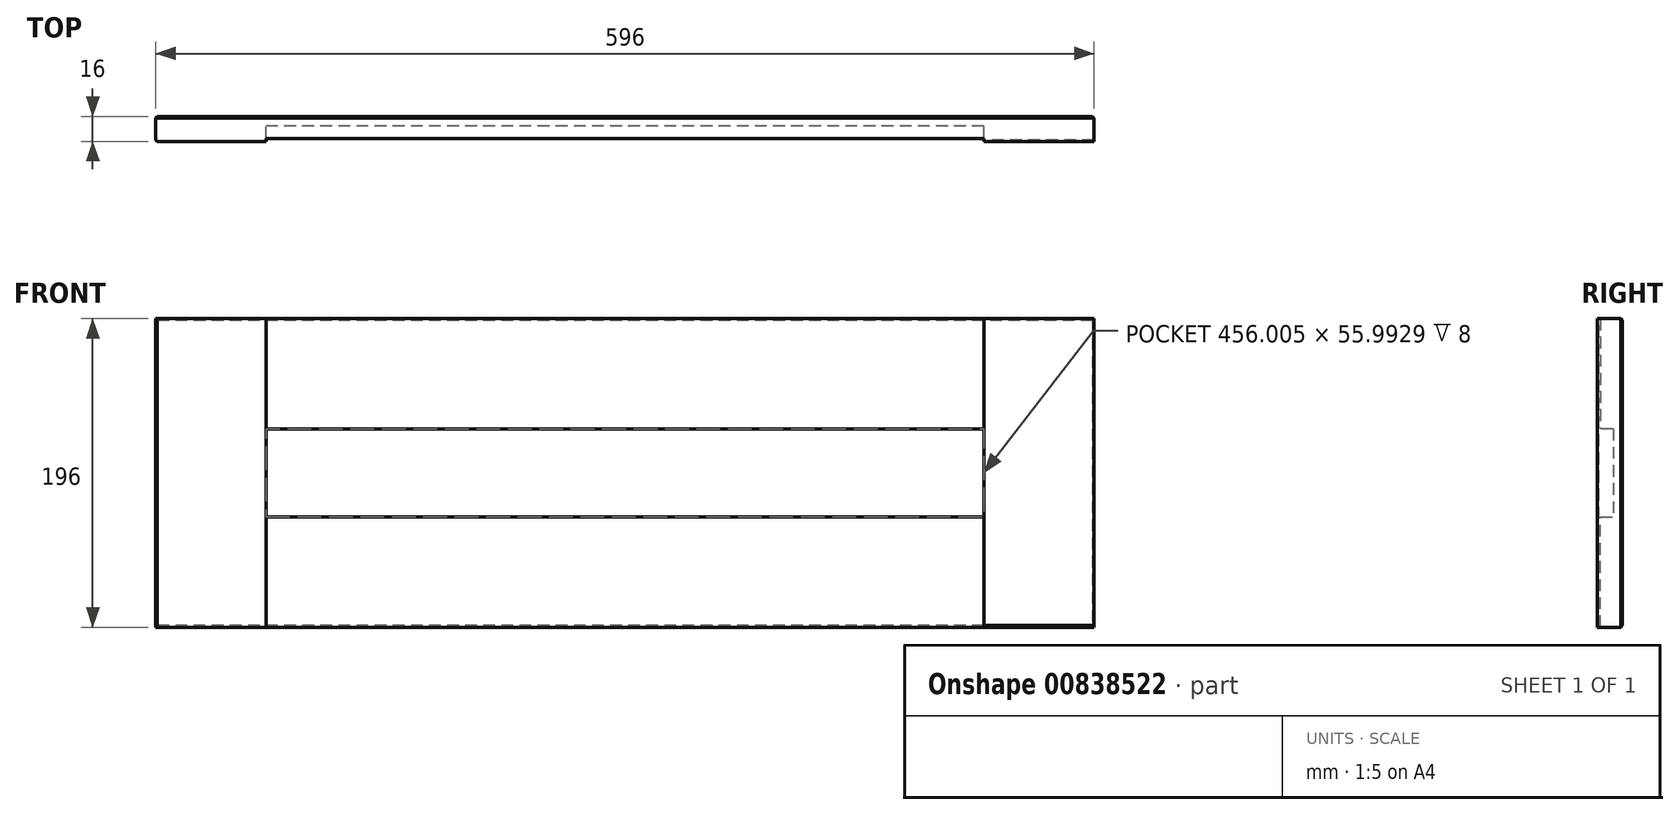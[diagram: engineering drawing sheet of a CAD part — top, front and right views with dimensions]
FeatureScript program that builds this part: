
annotation { "Feature Type Name" : "Feature", "Feature Type Description" : "" }
export const myFeature = defineFeature(function(context is Context, id is Id, definition is map)
    precondition{}
    {
        {
            var Q0;
            Q0=qCreatedBy(makeId("Front.planeOp"),FACE);
            var sketch = newSketch(context, id + "F0", { "sketchPlane" : qUnion([Q0])});
            skLineSegment(sketch, "E0.bottom", {"start": v(0, 0) * mm, "end": v(35.9, 0) * mm});
            skLineSegment(sketch, "E0.top", {"start": v(0, 30.12) * mm, "end": v(35.9, 30.12) * mm});
            skLineSegment(sketch, "E0.left", {"start": v(0, 0) * mm, "end": v(0, 30.12) * mm});
            skLineSegment(sketch, "E0.right", {"start": v(35.9, 0) * mm, "end": v(35.9, 30.12) * mm});
            skSolve(sketch);
        }
        {
            var Q0;
            Q0=makeQuery(id+"F0.imprint","IMPRINT",FACE,{"disambiguationData":[TD([[makeQuery(id+"F0.imprint","IMPRINT",EDGE,{"derivedFrom":sQuery(id+"F0.wireOp",EDGE,"E0.bottom")}),1.0]])]});
            extrude(context, id + "F1", {"entities" : qUnion([Q0]), "depth" : 16 * mm, "offsetDistance" : 25.4 * mm});
        }
        {
            var Q0;
            Q0=makeQuery(id+"F1.opExtrude","SWEPT_FACE",FACE,{"disambiguationData":[OSD([sQuery(id+"F0.wireOp",EDGE,"E0.left")])]});
            extrude(context, id + "F2", {"entities" : qUnion([Q0]), "operationType" : NewBodyOperationType.ADD, "oppositeDirection" : true, "depth" : 196 * mm, "offsetDistance" : 25 * mm});
        }
        {
            var Q0;
            {var subQ0=sQuery(id+"F0.wireOp",EDGE,"E0.bottom");Q0=makeQuery(id+"F2.boolean.opBoolean","MERGE",FACE,{"derivedFrom":[makeQuery(id+"F1.opExtrude","SWEPT_FACE",FACE,{"disambiguationData":[OSD([subQ0])]}),makeQuery(id+"F2.opExtrude","SWEPT_FACE",FACE,{"disambiguationData":[OSD([subQ0,sQuery(id+"F0.wireOp",EDGE,"E0.left")])]})]});}
            extrude(context, id + "F3", {"entities" : qUnion([Q0]), "operationType" : NewBodyOperationType.ADD, "oppositeDirection" : true, "depth" : 796 * mm, "offsetDistance" : 25 * mm});
        }
        {
            var Q0;
            {var subQ0=sQuery(id+"F0.wireOp",EDGE,"E0.left");var subQ1=sQuery(id+"F0.wireOp",EDGE,"E0.bottom");Q0=makeQuery(id+"F3.boolean.opBoolean","MERGE",FACE,{"derivedFrom":[makeQuery(id+"F2.boolean.opBoolean","MERGE",FACE,{"derivedFrom":[makeQuery(id+"F1.opExtrude","CAP_FACE",FACE,{"disambiguationData":[OSD([subQ1,sQuery(id+"F0.wireOp",EDGE,"E0.top"),subQ0,sQuery(id+"F0.wireOp",EDGE,"E0.right")])],"isStart":false}),makeQuery(id+"F2.opExtrude","SWEPT_FACE",FACE,{"disambiguationData":[OSD([subQ0]),TDD([makeQuery(id+"F1.opExtrude","CAP_EDGE",EDGE,{"disambiguationData":[OSD([subQ0])],"isStart":false})])]})]}),makeQuery(id+"F3.opExtrude","SWEPT_FACE",FACE,{"disambiguationData":[OSD([subQ1,subQ0]),TDD([makeQuery(id+"F2.boolean.opBoolean","MERGE",EDGE,{"derivedFrom":[makeQuery(id+"F1.opExtrude","CAP_EDGE",EDGE,{"disambiguationData":[OSD([subQ1])],"isStart":false}),makeQuery(id+"F2.opExtrude","SWEPT_EDGE",EDGE,{"disambiguationData":[OSD([subQ1,subQ0]),TDD([makeQuery(id+"F1.opExtrude","CAP_VERTEX",VERTEX,{"disambiguationData":[OSD([subQ1,subQ0])],"isStart":false})])]})]})])]})]});}
            var sketch = newSketch(context, id + "F4", { "sketchPlane" : qUnion([Q0])});
            skLineSegment(sketch, "E1.bottom", {"start": v(0, 796) * mm, "end": v(42.19, 796) * mm});
            skLineSegment(sketch, "E1.top", {"start": v(0, 751.57) * mm, "end": v(42.19, 751.57) * mm});
            skLineSegment(sketch, "E1.left", {"start": v(0, 796) * mm, "end": v(0, 751.57) * mm});
            skLineSegment(sketch, "E1.right", {"start": v(42.19, 796) * mm, "end": v(42.19, 751.57) * mm});
            skLineSegment(sketch, "E2.bottom", {"start": v(196, 796) * mm, "end": v(153.6, 796) * mm});
            skLineSegment(sketch, "E2.top", {"start": v(196, 746.75) * mm, "end": v(153.6, 746.75) * mm});
            skLineSegment(sketch, "E2.left", {"start": v(196, 796) * mm, "end": v(196, 746.75) * mm});
            skLineSegment(sketch, "E2.right", {"start": v(153.6, 796) * mm, "end": v(153.6, 746.75) * mm});
            skSolve(sketch);
        }
        {
            var Q0;
            Q0=makeQuery(id+"F4.imprint","IMPRINT",FACE,{"disambiguationData":[TD([[makeQuery(id+"F4.imprint","IMPRINT",EDGE,{"derivedFrom":sQuery(id+"F4.wireOp",EDGE,"E1.bottom")}),-1.0]])]});
            var Q1;
            Q1=makeQuery(id+"F4.imprint","IMPRINT",FACE,{"disambiguationData":[TD([[makeQuery(id+"F4.imprint","IMPRINT",EDGE,{"derivedFrom":sQuery(id+"F4.wireOp",EDGE,"E2.bottom")}),-1.0]])]});
            extrude(context, id + "F5", {"entities" : qUnion([Q0, Q1]), "operationType" : NewBodyOperationType.ADD, "depth" : 25 * mm, "offsetDistance" : 25 * mm});
        }
        {
            var Q0;
            {var subQ0=sQuery(id+"F0.wireOp",EDGE,"E0.left");var subQ1=sQuery(id+"F0.wireOp",EDGE,"E0.bottom");Q0=makeQuery(id+"F3.boolean.opBoolean","MERGE",FACE,{"derivedFrom":[makeQuery(id+"F2.boolean.opBoolean","MERGE",FACE,{"derivedFrom":[makeQuery(id+"F1.opExtrude","CAP_FACE",FACE,{"disambiguationData":[OSD([subQ1,sQuery(id+"F0.wireOp",EDGE,"E0.top"),subQ0,sQuery(id+"F0.wireOp",EDGE,"E0.right")])],"isStart":false}),makeQuery(id+"F2.opExtrude","SWEPT_FACE",FACE,{"disambiguationData":[OSD([subQ0]),TDD([makeQuery(id+"F1.opExtrude","CAP_EDGE",EDGE,{"disambiguationData":[OSD([subQ0])],"isStart":false})])]})]}),makeQuery(id+"F3.opExtrude","SWEPT_FACE",FACE,{"disambiguationData":[OSD([subQ1,subQ0]),TDD([makeQuery(id+"F2.boolean.opBoolean","MERGE",EDGE,{"derivedFrom":[makeQuery(id+"F1.opExtrude","CAP_EDGE",EDGE,{"disambiguationData":[OSD([subQ1])],"isStart":false}),makeQuery(id+"F2.opExtrude","SWEPT_EDGE",EDGE,{"disambiguationData":[OSD([subQ1,subQ0]),TDD([makeQuery(id+"F1.opExtrude","CAP_VERTEX",VERTEX,{"disambiguationData":[OSD([subQ1,subQ0])],"isStart":false})])]})]})])]})]});}
            var sketch = newSketch(context, id + "F6", { "sketchPlane" : qUnion([Q0])});
            skLineSegment(sketch, "E3.bottom", {"start": v(196, 0) * mm, "end": v(163.38, 0) * mm});
            skLineSegment(sketch, "E3.top", {"start": v(196, 46.55) * mm, "end": v(163.38, 46.55) * mm});
            skLineSegment(sketch, "E3.left", {"start": v(196, 0) * mm, "end": v(196, 46.55) * mm});
            skLineSegment(sketch, "E3.right", {"start": v(163.38, 0) * mm, "end": v(163.38, 46.55) * mm});
            skLineSegment(sketch, "E4.bottom", {"start": v(0, 0) * mm, "end": v(50.28, 0) * mm});
            skLineSegment(sketch, "E4.top", {"start": v(0, 44.4) * mm, "end": v(50.28, 44.4) * mm});
            skLineSegment(sketch, "E4.left", {"start": v(0, 0) * mm, "end": v(0, 44.4) * mm});
            skLineSegment(sketch, "E4.right", {"start": v(50.28, 0) * mm, "end": v(50.28, 44.4) * mm});
            skSolve(sketch);
        }
        {
            var Q0;
            Q0=makeQuery(id+"F6.imprint","IMPRINT",FACE,{"disambiguationData":[TD([[makeQuery(id+"F6.imprint","IMPRINT",EDGE,{"derivedFrom":sQuery(id+"F6.wireOp",EDGE,"E3.bottom")}),1.0]])]});
            var Q1;
            Q1=makeQuery(id+"F6.imprint","IMPRINT",FACE,{"disambiguationData":[TD([[makeQuery(id+"F6.imprint","IMPRINT",EDGE,{"derivedFrom":sQuery(id+"F6.wireOp",EDGE,"E4.bottom")}),1.0]])]});
            extrude(context, id + "F7", {"entities" : qUnion([Q0, Q1]), "operationType" : NewBodyOperationType.ADD, "depth" : 25 * mm, "offsetDistance" : 25 * mm});
        }
        {
            var Q0;
            Q0=makeQuery(id+"F7.opExtrude","SWEPT_FACE",FACE,{"disambiguationData":[OSD([sQuery(id+"F6.wireOp",EDGE,"E4.right")])]});
            extrude(context, id + "F8", {"entities" : qUnion([Q0]), "operationType" : NewBodyOperationType.ADD, "depth" : 19.72 * mm, "offsetDistance" : 25 * mm});
        }
        {
            var Q0;
            {var subQ0=sQuery(id+"F6.wireOp",EDGE,"E4.top");Q0=makeQuery(id+"F8.boolean.opBoolean","MERGE",FACE,{"derivedFrom":[makeQuery(id+"F7.opExtrude","SWEPT_FACE",FACE,{"disambiguationData":[OSD([subQ0])]}),makeQuery(id+"F8.opExtrude","SWEPT_FACE",FACE,{"disambiguationData":[OSD([subQ0,sQuery(id+"F6.wireOp",EDGE,"E4.right")])]})]});}
            extrude(context, id + "F9", {"entities" : qUnion([Q0]), "operationType" : NewBodyOperationType.ADD, "depth" : 25.6 * mm, "offsetDistance" : 25 * mm});
        }
        {
            var Q0;
            Q0=makeQuery(id+"F7.opExtrude","SWEPT_FACE",FACE,{"disambiguationData":[OSD([sQuery(id+"F6.wireOp",EDGE,"E3.right")])]});
            extrude(context, id + "F10", {"entities" : qUnion([Q0]), "operationType" : NewBodyOperationType.ADD, "depth" : 37.38 * mm, "offsetDistance" : 25 * mm});
        }
        {
            var Q0;
            {var subQ0=sQuery(id+"F6.wireOp",EDGE,"E3.top");Q0=makeQuery(id+"F10.boolean.opBoolean","MERGE",FACE,{"derivedFrom":[makeQuery(id+"F7.opExtrude","SWEPT_FACE",FACE,{"disambiguationData":[OSD([subQ0])]}),makeQuery(id+"F10.opExtrude","SWEPT_FACE",FACE,{"disambiguationData":[OSD([subQ0,sQuery(id+"F6.wireOp",EDGE,"E3.right")])]})]});}
            extrude(context, id + "F11", {"entities" : qUnion([Q0]), "operationType" : NewBodyOperationType.ADD, "depth" : 23.45 * mm, "offsetDistance" : 25 * mm});
        }
        {
            var Q0;
            Q0=makeQuery(id+"F5.opExtrude","SWEPT_FACE",FACE,{"disambiguationData":[OSD([sQuery(id+"F4.wireOp",EDGE,"E1.right")])]});
            extrude(context, id + "F12", {"entities" : qUnion([Q0]), "operationType" : NewBodyOperationType.ADD, "depth" : 27.8 * mm, "offsetDistance" : 25 * mm});
        }
        {
            var Q0;
            {var subQ0=sQuery(id+"F4.wireOp",EDGE,"E1.top");Q0=makeQuery(id+"F12.boolean.opBoolean","MERGE",FACE,{"derivedFrom":[makeQuery(id+"F5.opExtrude","SWEPT_FACE",FACE,{"disambiguationData":[OSD([subQ0])]}),makeQuery(id+"F12.opExtrude","SWEPT_FACE",FACE,{"disambiguationData":[OSD([subQ0,sQuery(id+"F4.wireOp",EDGE,"E1.right")])]})]});}
            extrude(context, id + "F13", {"entities" : qUnion([Q0]), "operationType" : NewBodyOperationType.ADD, "depth" : 25.57 * mm, "offsetDistance" : 25 * mm});
        }
        {
            var Q0;
            Q0=makeQuery(id+"F5.opExtrude","SWEPT_FACE",FACE,{"disambiguationData":[OSD([sQuery(id+"F4.wireOp",EDGE,"E2.top")])]});
            extrude(context, id + "F14", {"entities" : qUnion([Q0]), "operationType" : NewBodyOperationType.ADD, "depth" : 20.75 * mm, "offsetDistance" : 25 * mm});
        }
        {
            var Q0;
            {var subQ0=sQuery(id+"F4.wireOp",EDGE,"E2.right");Q0=makeQuery(id+"F14.boolean.opBoolean","MERGE",FACE,{"derivedFrom":[makeQuery(id+"F5.opExtrude","SWEPT_FACE",FACE,{"disambiguationData":[OSD([subQ0])]}),makeQuery(id+"F14.opExtrude","SWEPT_FACE",FACE,{"disambiguationData":[OSD([sQuery(id+"F4.wireOp",EDGE,"E2.top"),subQ0])]})]});}
            extrude(context, id + "F15", {"entities" : qUnion([Q0]), "operationType" : NewBodyOperationType.ADD, "depth" : 27.6 * mm, "offsetDistance" : 25 * mm});
        }
        {
            var Q0;
            {var subQ0=sQuery(id+"F0.wireOp",EDGE,"E0.left");var subQ1=sQuery(id+"F0.wireOp",EDGE,"E0.bottom");Q0=makeQuery(id+"F3.boolean.opBoolean","MERGE",FACE,{"derivedFrom":[makeQuery(id+"F2.boolean.opBoolean","MERGE",FACE,{"derivedFrom":[makeQuery(id+"F1.opExtrude","CAP_FACE",FACE,{"disambiguationData":[OSD([subQ1,sQuery(id+"F0.wireOp",EDGE,"E0.top"),subQ0,sQuery(id+"F0.wireOp",EDGE,"E0.right")])],"isStart":false}),makeQuery(id+"F2.opExtrude","SWEPT_FACE",FACE,{"disambiguationData":[OSD([subQ0]),TDD([makeQuery(id+"F1.opExtrude","CAP_EDGE",EDGE,{"disambiguationData":[OSD([subQ0])],"isStart":false})])]})]}),makeQuery(id+"F3.opExtrude","SWEPT_FACE",FACE,{"disambiguationData":[OSD([subQ1,subQ0]),TDD([makeQuery(id+"F2.boolean.opBoolean","MERGE",EDGE,{"derivedFrom":[makeQuery(id+"F1.opExtrude","CAP_EDGE",EDGE,{"disambiguationData":[OSD([subQ1])],"isStart":false}),makeQuery(id+"F2.opExtrude","SWEPT_EDGE",EDGE,{"disambiguationData":[OSD([subQ1,subQ0]),TDD([makeQuery(id+"F1.opExtrude","CAP_VERTEX",VERTEX,{"disambiguationData":[OSD([subQ1,subQ0])],"isStart":false})])]})]})])]})]});}
            var sketch = newSketch(context, id + "F16", { "sketchPlane" : qUnion([Q0])});
            skLineSegment(sketch, "E5.bottom", {"start": v(70, 726) * mm, "end": v(126, 726) * mm});
            skLineSegment(sketch, "E5.top", {"start": v(70, 70) * mm, "end": v(126, 70) * mm});
            skLineSegment(sketch, "E5.left", {"start": v(70, 726) * mm, "end": v(70, 70) * mm});
            skLineSegment(sketch, "E5.right", {"start": v(126, 726) * mm, "end": v(126, 70) * mm});
            skSolve(sketch);
        }
        {
            var Q0;
            Q0=makeQuery(id+"F16.imprint","IMPRINT",FACE,{"disambiguationData":[TD([[makeQuery(id+"F16.imprint","IMPRINT",EDGE,{"derivedFrom":sQuery(id+"F16.wireOp",EDGE,"E5.top")}),1.0]])]});
            extrude(context, id + "F17", {"entities" : qUnion([Q0]), "operationType" : NewBodyOperationType.REMOVE, "oppositeDirection" : true, "depth" : 10 * mm, "offsetDistance" : 25 * mm});
        }
        {
            var Q0;
            {var subQ2=sQuery(id+"F0.wireOp",EDGE,"E0.left");var subQ3=sQuery(id+"F0.wireOp",EDGE,"E0.bottom");var subQ4=makeQuery(id+"F1.opExtrude","CAP_FACE",FACE,{"disambiguationData":[OSD([subQ3,sQuery(id+"F0.wireOp",EDGE,"E0.top"),subQ2,sQuery(id+"F0.wireOp",EDGE,"E0.right")])],"isStart":false});var subQ7=makeQuery(id+"F3.opExtrude","SWEPT_FACE",FACE,{"disambiguationData":[OSD([subQ3,subQ2]),TDD([makeQuery(id+"F2.boolean.opBoolean","MERGE",EDGE,{"derivedFrom":[makeQuery(id+"F1.opExtrude","CAP_EDGE",EDGE,{"disambiguationData":[OSD([subQ3])],"isStart":false}),makeQuery(id+"F2.opExtrude","SWEPT_EDGE",EDGE,{"disambiguationData":[OSD([subQ3,subQ2]),TDD([makeQuery(id+"F1.opExtrude","CAP_VERTEX",VERTEX,{"disambiguationData":[OSD([subQ3,subQ2])],"isStart":false})])]})]})])]});var subQ8=makeQuery(id+"F2.opExtrude","SWEPT_FACE",FACE,{"disambiguationData":[OSD([subQ2]),TDD([makeQuery(id+"F1.opExtrude","CAP_EDGE",EDGE,{"disambiguationData":[OSD([subQ2])],"isStart":false})])]});Q0=makeQuery(id+"F17.boolean.opBoolean","SPLIT",FACE,{"disambiguationData":[TD([makeQuery(id+"F1.opExtrude","SWEPT_FACE",FACE,{"disambiguationData":[OSD([subQ3])]})])],"derivedFrom":makeQuery(id+"F3.boolean.opBoolean","MERGE",FACE,{"derivedFrom":[makeQuery(id+"F2.boolean.opBoolean","MERGE",FACE,{"derivedFrom":[subQ4,subQ8]}),subQ7]})});}
            var Q1;
            {var subQ2=sQuery(id+"F4.wireOp",EDGE,"E1.bottom");var subQ3=sQuery(id+"F0.wireOp",EDGE,"E0.left");var subQ4=sQuery(id+"F0.wireOp",EDGE,"E0.bottom");var subQ6=makeQuery(id+"F1.opExtrude","CAP_FACE",FACE,{"disambiguationData":[OSD([subQ4,sQuery(id+"F0.wireOp",EDGE,"E0.top"),subQ3,sQuery(id+"F0.wireOp",EDGE,"E0.right")])],"isStart":false});var subQ7=makeQuery(id+"F2.opExtrude","SWEPT_FACE",FACE,{"disambiguationData":[OSD([subQ3]),TDD([makeQuery(id+"F1.opExtrude","CAP_EDGE",EDGE,{"disambiguationData":[OSD([subQ3])],"isStart":false})])]});var subQ8=makeQuery(id+"F3.opExtrude","SWEPT_FACE",FACE,{"disambiguationData":[OSD([subQ4,subQ3]),TDD([makeQuery(id+"F2.boolean.opBoolean","MERGE",EDGE,{"derivedFrom":[makeQuery(id+"F1.opExtrude","CAP_EDGE",EDGE,{"disambiguationData":[OSD([subQ4])],"isStart":false}),makeQuery(id+"F2.opExtrude","SWEPT_EDGE",EDGE,{"disambiguationData":[OSD([subQ4,subQ3]),TDD([makeQuery(id+"F1.opExtrude","CAP_VERTEX",VERTEX,{"disambiguationData":[OSD([subQ4,subQ3])],"isStart":false})])]})]})])]});Q1=makeQuery(id+"F17.boolean.opBoolean","SPLIT",FACE,{"disambiguationData":[TD([makeQuery(id+"F5.opExtrude","SWEPT_FACE",FACE,{"disambiguationData":[OSD([subQ2])]})])],"derivedFrom":makeQuery(id+"F3.boolean.opBoolean","MERGE",FACE,{"derivedFrom":[makeQuery(id+"F2.boolean.opBoolean","MERGE",FACE,{"derivedFrom":[subQ6,subQ7]}),subQ8]})});}
            extrude(context, id + "F18", {"entities" : qUnion([Q0, Q1]), "operationType" : NewBodyOperationType.REMOVE, "oppositeDirection" : true, "depth" : 2 * mm, "offsetDistance" : 25 * mm});
        }
        {
            var Q0;
            {var subQ0=sQuery(id+"F4.wireOp",EDGE,"E1.right");var subQ1=sQuery(id+"F4.wireOp",EDGE,"E1.top");Q0=makeQuery(id+"F13.boolean.opBoolean","MERGE",FACE,{"derivedFrom":[makeQuery(id+"F12.boolean.opBoolean","MERGE",FACE,{"derivedFrom":[makeQuery(id+"F5.opExtrude","CAP_FACE",FACE,{"disambiguationData":[OSD([sQuery(id+"F4.wireOp",EDGE,"E1.bottom"),subQ1,sQuery(id+"F4.wireOp",EDGE,"E1.left"),subQ0])],"isStart":false}),makeQuery(id+"F12.opExtrude","SWEPT_FACE",FACE,{"disambiguationData":[OSD([subQ0]),TDD([makeQuery(id+"F5.opExtrude","CAP_EDGE",EDGE,{"disambiguationData":[OSD([subQ0])],"isStart":false})])]})]}),makeQuery(id+"F13.opExtrude","SWEPT_FACE",FACE,{"disambiguationData":[OSD([subQ1,subQ0]),TDD([makeQuery(id+"F12.boolean.opBoolean","MERGE",EDGE,{"derivedFrom":[makeQuery(id+"F5.opExtrude","CAP_EDGE",EDGE,{"disambiguationData":[OSD([subQ1])],"isStart":false}),makeQuery(id+"F12.opExtrude","SWEPT_EDGE",EDGE,{"disambiguationData":[OSD([subQ1,subQ0]),TDD([makeQuery(id+"F5.opExtrude","CAP_VERTEX",VERTEX,{"disambiguationData":[OSD([subQ1,subQ0])],"isStart":false})])]})]})])]})]});}
            var Q1;
            {var subQ0=sQuery(id+"F4.wireOp",EDGE,"E2.right");var subQ1=sQuery(id+"F4.wireOp",EDGE,"E2.top");Q1=makeQuery(id+"F15.boolean.opBoolean","MERGE",FACE,{"derivedFrom":[makeQuery(id+"F14.boolean.opBoolean","MERGE",FACE,{"derivedFrom":[makeQuery(id+"F5.opExtrude","CAP_FACE",FACE,{"disambiguationData":[OSD([sQuery(id+"F4.wireOp",EDGE,"E2.bottom"),subQ1,sQuery(id+"F4.wireOp",EDGE,"E2.left"),subQ0])],"isStart":false}),makeQuery(id+"F14.opExtrude","SWEPT_FACE",FACE,{"disambiguationData":[OSD([subQ1]),TDD([makeQuery(id+"F5.opExtrude","CAP_EDGE",EDGE,{"disambiguationData":[OSD([subQ1])],"isStart":false})])]})]}),makeQuery(id+"F15.opExtrude","SWEPT_FACE",FACE,{"disambiguationData":[OSD([subQ1,subQ0]),TDD([makeQuery(id+"F14.boolean.opBoolean","MERGE",EDGE,{"derivedFrom":[makeQuery(id+"F5.opExtrude","CAP_EDGE",EDGE,{"disambiguationData":[OSD([subQ0])],"isStart":false}),makeQuery(id+"F14.opExtrude","SWEPT_EDGE",EDGE,{"disambiguationData":[OSD([subQ1,subQ0]),TDD([makeQuery(id+"F5.opExtrude","CAP_VERTEX",VERTEX,{"disambiguationData":[OSD([subQ1,subQ0])],"isStart":false})])]})]})])]})]});}
            var Q2;
            {var subQ0=sQuery(id+"F6.wireOp",EDGE,"E4.right");var subQ1=sQuery(id+"F6.wireOp",EDGE,"E4.top");Q2=makeQuery(id+"F9.boolean.opBoolean","MERGE",FACE,{"derivedFrom":[makeQuery(id+"F8.boolean.opBoolean","MERGE",FACE,{"derivedFrom":[makeQuery(id+"F7.opExtrude","CAP_FACE",FACE,{"disambiguationData":[OSD([sQuery(id+"F6.wireOp",EDGE,"E4.bottom"),subQ1,sQuery(id+"F6.wireOp",EDGE,"E4.left"),subQ0])],"isStart":false}),makeQuery(id+"F8.opExtrude","SWEPT_FACE",FACE,{"disambiguationData":[OSD([subQ0]),TDD([makeQuery(id+"F7.opExtrude","CAP_EDGE",EDGE,{"disambiguationData":[OSD([subQ0])],"isStart":false})])]})]}),makeQuery(id+"F9.opExtrude","SWEPT_FACE",FACE,{"disambiguationData":[OSD([subQ1,subQ0]),TDD([makeQuery(id+"F8.boolean.opBoolean","MERGE",EDGE,{"derivedFrom":[makeQuery(id+"F7.opExtrude","CAP_EDGE",EDGE,{"disambiguationData":[OSD([subQ1])],"isStart":false}),makeQuery(id+"F8.opExtrude","SWEPT_EDGE",EDGE,{"disambiguationData":[OSD([subQ1,subQ0]),TDD([makeQuery(id+"F7.opExtrude","CAP_VERTEX",VERTEX,{"disambiguationData":[OSD([subQ1,subQ0])],"isStart":false})])]})]})])]})]});}
            var Q3;
            {var subQ0=sQuery(id+"F6.wireOp",EDGE,"E3.right");var subQ1=sQuery(id+"F6.wireOp",EDGE,"E3.top");Q3=makeQuery(id+"F11.boolean.opBoolean","MERGE",FACE,{"derivedFrom":[makeQuery(id+"F10.boolean.opBoolean","MERGE",FACE,{"derivedFrom":[makeQuery(id+"F7.opExtrude","CAP_FACE",FACE,{"disambiguationData":[OSD([sQuery(id+"F6.wireOp",EDGE,"E3.bottom"),subQ1,sQuery(id+"F6.wireOp",EDGE,"E3.left"),subQ0])],"isStart":false}),makeQuery(id+"F10.opExtrude","SWEPT_FACE",FACE,{"disambiguationData":[OSD([subQ0]),TDD([makeQuery(id+"F7.opExtrude","CAP_EDGE",EDGE,{"disambiguationData":[OSD([subQ0])],"isStart":false})])]})]}),makeQuery(id+"F11.opExtrude","SWEPT_FACE",FACE,{"disambiguationData":[OSD([subQ1,subQ0]),TDD([makeQuery(id+"F10.boolean.opBoolean","MERGE",EDGE,{"derivedFrom":[makeQuery(id+"F7.opExtrude","CAP_EDGE",EDGE,{"disambiguationData":[OSD([subQ1])],"isStart":false}),makeQuery(id+"F10.opExtrude","SWEPT_EDGE",EDGE,{"disambiguationData":[OSD([subQ1,subQ0]),TDD([makeQuery(id+"F7.opExtrude","CAP_VERTEX",VERTEX,{"disambiguationData":[OSD([subQ1,subQ0])],"isStart":false})])]})]})])]})]});}
            extrude(context, id + "F19", {"entities" : qUnion([Q0, Q1, Q2, Q3]), "operationType" : NewBodyOperationType.REMOVE, "oppositeDirection" : true, "depth" : 25 * mm, "offsetDistance" : 25 * mm});
        }
        {
            var Q0;
            {var subQ0=sQuery(id+"F4.wireOp",EDGE,"E2.left");var subQ1=sQuery(id+"F0.wireOp",EDGE,"E0.left");var subQ2=sQuery(id+"F0.wireOp",EDGE,"E0.bottom");var subQ3=sQuery(id+"F6.wireOp",EDGE,"E3.left");Q0=makeQuery(id+"F14.boolean.opBoolean","MERGE",FACE,{"derivedFrom":[makeQuery(id+"F11.boolean.opBoolean","MERGE",FACE,{"derivedFrom":[makeQuery(id+"F7.boolean.opBoolean","MERGE",FACE,{"derivedFrom":[makeQuery(id+"F5.boolean.opBoolean","MERGE",FACE,{"derivedFrom":[makeQuery(id+"F3.boolean.opBoolean","MERGE",FACE,{"derivedFrom":[makeQuery(id+"F2.opExtrude","CAP_FACE",FACE,{"disambiguationData":[OSD([subQ1])],"isStart":false}),makeQuery(id+"F3.opExtrude","SWEPT_FACE",FACE,{"disambiguationData":[OSD([subQ2,subQ1]),TDD([makeQuery(id+"F2.opExtrude","CAP_EDGE",EDGE,{"disambiguationData":[OSD([subQ2,subQ1])],"isStart":false})])]})]}),makeQuery(id+"F5.opExtrude","SWEPT_FACE",FACE,{"disambiguationData":[OSD([subQ0])]})]}),makeQuery(id+"F7.opExtrude","SWEPT_FACE",FACE,{"disambiguationData":[OSD([subQ3])]})]}),makeQuery(id+"F11.opExtrude","SWEPT_FACE",FACE,{"disambiguationData":[OSD([subQ2,subQ1,sQuery(id+"F6.wireOp",EDGE,"E3.top"),subQ3])]})]}),makeQuery(id+"F14.opExtrude","SWEPT_FACE",FACE,{"disambiguationData":[OSD([subQ2,subQ1,sQuery(id+"F4.wireOp",EDGE,"E2.top"),subQ0])]})]});}
            extrude(context, id + "F20", {"entities" : qUnion([Q0]), "operationType" : NewBodyOperationType.ADD, "depth" : 200 * mm, "offsetDistance" : 25 * mm});
        }
        {
            var Q0;
            {var subQ0=sQuery(id+"F4.wireOp",EDGE,"E2.right");var subQ1=sQuery(id+"F4.wireOp",EDGE,"E2.top");Q0=makeQuery(id+"F18.boolean.opBoolean","MERGE",FACE,{"derivedFrom":[makeQuery(id+"F15.opExtrude","CAP_FACE",FACE,{"disambiguationData":[OSD([subQ1,subQ0])],"isStart":false}),makeQuery(id+"F18.opExtrude","SWEPT_FACE",FACE,{"disambiguationData":[OSD([subQ1,subQ0])]})]});}
            var Q1;
            {var subQ0=sQuery(id+"F6.wireOp",EDGE,"E3.right");var subQ1=sQuery(id+"F6.wireOp",EDGE,"E3.top");Q1=makeQuery(id+"F18.boolean.opBoolean","MERGE",FACE,{"derivedFrom":[makeQuery(id+"F11.boolean.opBoolean","MERGE",FACE,{"derivedFrom":[makeQuery(id+"F10.opExtrude","CAP_FACE",FACE,{"disambiguationData":[OSD([subQ0])],"isStart":false}),makeQuery(id+"F11.opExtrude","SWEPT_FACE",FACE,{"disambiguationData":[OSD([subQ1,subQ0]),TDD([makeQuery(id+"F10.opExtrude","CAP_EDGE",EDGE,{"disambiguationData":[OSD([subQ1,subQ0])],"isStart":false})])]})]}),makeQuery(id+"F17.boolean.opBoolean","COPY",FACE,{"derivedFrom":makeQuery(id+"F17.opExtrude","SWEPT_FACE",FACE,{"disambiguationData":[OSD([sQuery(id+"F16.wireOp",EDGE,"E5.right")])]})}),makeQuery(id+"F18.opExtrude","SWEPT_FACE",FACE,{"disambiguationData":[OSD([subQ1,subQ0])]})]});}
            extrude(context, id + "F21", {"entities" : qUnion([Q0, Q1]), "operationType" : NewBodyOperationType.REMOVE, "oppositeDirection" : true, "depth" : 200 * mm, "offsetDistance" : 25 * mm});
        }
        {
            var Q0;
            {var subQ0=sQuery(id+"F4.wireOp",EDGE,"E2.bottom");var subQ1=sQuery(id+"F0.wireOp",EDGE,"E0.left");var subQ2=sQuery(id+"F0.wireOp",EDGE,"E0.bottom");var subQ3=sQuery(id+"F4.wireOp",EDGE,"E1.bottom");Q0=makeQuery(id+"F20.boolean.opBoolean","MERGE",FACE,{"derivedFrom":[makeQuery(id+"F15.boolean.opBoolean","MERGE",FACE,{"derivedFrom":[makeQuery(id+"F12.boolean.opBoolean","MERGE",FACE,{"derivedFrom":[makeQuery(id+"F5.boolean.opBoolean","MERGE",FACE,{"derivedFrom":[makeQuery(id+"F3.opExtrude","CAP_FACE",FACE,{"disambiguationData":[OSD([subQ2,subQ1])],"isStart":false}),makeQuery(id+"F5.opExtrude","SWEPT_FACE",FACE,{"disambiguationData":[OSD([subQ3])]}),makeQuery(id+"F5.opExtrude","SWEPT_FACE",FACE,{"disambiguationData":[OSD([subQ0])]})]}),makeQuery(id+"F12.opExtrude","SWEPT_FACE",FACE,{"disambiguationData":[OSD([subQ2,subQ1,subQ3,sQuery(id+"F4.wireOp",EDGE,"E1.right")])]})]}),makeQuery(id+"F15.opExtrude","SWEPT_FACE",FACE,{"disambiguationData":[OSD([subQ2,subQ1,subQ0,sQuery(id+"F4.wireOp",EDGE,"E2.right")])]})]}),makeQuery(id+"F20.opExtrude","SWEPT_FACE",FACE,{"disambiguationData":[OSD([subQ2,subQ1,subQ0,sQuery(id+"F4.wireOp",EDGE,"E2.left")])]})]});}
            extrude(context, id + "F22", {"entities" : qUnion([Q0]), "operationType" : NewBodyOperationType.ADD, "depth" : 200 * mm, "offsetDistance" : 25 * mm});
        }
        {
            var Q0;
            Q0=makeQuery(id+"F17.boolean.opBoolean","COPY",FACE,{"derivedFrom":makeQuery(id+"F17.opExtrude","SWEPT_FACE",FACE,{"disambiguationData":[OSD([sQuery(id+"F16.wireOp",EDGE,"E5.bottom")])]})});
            var Q1;
            {var subQ0=sQuery(id+"F16.wireOp",EDGE,"E5.right");var subQ1=sQuery(id+"F16.wireOp",EDGE,"E5.bottom");var subQ2=sQuery(id+"F4.wireOp",EDGE,"E2.right");var subQ3=sQuery(id+"F4.wireOp",EDGE,"E2.top");var subQ4=makeQuery(id+"F17.boolean.opBoolean","COPY",EDGE,{"derivedFrom":makeQuery(id+"F17.opExtrude","SWEPT_EDGE",EDGE,{"disambiguationData":[OSD([subQ3,subQ2,subQ1,subQ0])]})});Q1=makeQuery(id+"F21.boolean.opBoolean","COPY",FACE,{"derivedFrom":makeQuery(id+"F21.opExtrude","SWEPT_FACE",FACE,{"disambiguationData":[OSD([subQ3,subQ2,subQ1,subQ0]),TDD([makeQuery(id+"F18.boolean.opBoolean","MERGE",EDGE,{"derivedFrom":[subQ4,makeQuery(id+"F18.opExtrude","SWEPT_EDGE",EDGE,{"disambiguationData":[OSD([subQ3,subQ2,subQ1,subQ0])]})]}),makeQuery(id+"F18.boolean.opBoolean","SPLIT",EDGE,{"derivedFrom":subQ4})])]})});}
            extrude(context, id + "F23", {"entities" : qUnion([Q0, Q1]), "operationType" : NewBodyOperationType.REMOVE, "oppositeDirection" : true, "depth" : 200 * mm, "offsetDistance" : 25 * mm});
        }
        {
            var Q0;
            Q0=makeQuery(id+"F23.boolean.opBoolean","COPY",FACE,{"derivedFrom":makeQuery(id+"F23.opExtrude","CAP_FACE",FACE,{"disambiguationData":[OSD([sQuery(id+"F16.wireOp",EDGE,"E5.bottom")])],"isStart":false})});
            var Q1;
            Q1=makeQuery(id+"F23.boolean.opBoolean","COPY",FACE,{"derivedFrom":makeQuery(id+"F23.opExtrude","CAP_FACE",FACE,{"disambiguationData":[OSD([sQuery(id+"F4.wireOp",EDGE,"E2.top"),sQuery(id+"F4.wireOp",EDGE,"E2.right"),sQuery(id+"F16.wireOp",EDGE,"E5.bottom"),sQuery(id+"F16.wireOp",EDGE,"E5.right")])],"isStart":false})});
            extrude(context, id + "F24", {"entities" : qUnion([Q0, Q1]), "operationType" : NewBodyOperationType.ADD, "depth" : 600 * mm, "offsetDistance" : 25 * mm});
        }
        {
            var Q0;
            Q0=makeQuery(id+"F22.opExtrude","CAP_FACE",FACE,{"disambiguationData":[OSD([sQuery(id+"F0.wireOp",EDGE,"E0.bottom"),sQuery(id+"F0.wireOp",EDGE,"E0.left"),sQuery(id+"F4.wireOp",EDGE,"E1.bottom"),sQuery(id+"F4.wireOp",EDGE,"E1.right"),sQuery(id+"F4.wireOp",EDGE,"E2.bottom"),sQuery(id+"F4.wireOp",EDGE,"E2.left"),sQuery(id+"F4.wireOp",EDGE,"E2.right")])],"isStart":false});
            extrude(context, id + "F25", {"entities" : qUnion([Q0]), "operationType" : NewBodyOperationType.REMOVE, "oppositeDirection" : true, "depth" : 600 * mm, "offsetDistance" : 25 * mm, "hasDraft" : true, "draftAngle" : 3 * degree});
        }
        {
            var Q0;
            {var subQ0=sQuery(id+"F4.wireOp",EDGE,"E2.left");var subQ1=sQuery(id+"F0.wireOp",EDGE,"E0.left");var subQ2=sQuery(id+"F0.wireOp",EDGE,"E0.bottom");Q0=makeQuery(id+"F22.boolean.opBoolean","MERGE",FACE,{"derivedFrom":[makeQuery(id+"F20.opExtrude","CAP_FACE",FACE,{"disambiguationData":[OSD([subQ2,subQ1,sQuery(id+"F4.wireOp",EDGE,"E2.top"),subQ0,sQuery(id+"F6.wireOp",EDGE,"E3.top"),sQuery(id+"F6.wireOp",EDGE,"E3.left")])],"isStart":false}),makeQuery(id+"F22.opExtrude","SWEPT_FACE",FACE,{"disambiguationData":[OSD([subQ2,subQ1,sQuery(id+"F4.wireOp",EDGE,"E2.bottom"),subQ0])]})]});}
            extrude(context, id + "F26", {"entities" : qUnion([Q0]), "operationType" : NewBodyOperationType.ADD, "depth" : 200 * mm, "offsetDistance" : 25 * mm, "hasSecondDirection" : true, "secondDirectionOppositeDirection" : true, "secondDirectionDepth" : 25 * mm});
        }
        {
            var Q0;
            {var subQ0=sQuery(id+"F16.wireOp",EDGE,"E5.right");var subQ1=sQuery(id+"F16.wireOp",EDGE,"E5.bottom");var subQ2=sQuery(id+"F4.wireOp",EDGE,"E2.right");var subQ3=sQuery(id+"F4.wireOp",EDGE,"E2.top");var subQ4=makeQuery(id+"F17.boolean.opBoolean","COPY",EDGE,{"derivedFrom":makeQuery(id+"F17.opExtrude","SWEPT_EDGE",EDGE,{"disambiguationData":[OSD([subQ3,subQ2,subQ1,subQ0])]})});Q0=makeQuery(id+"F23.boolean.opBoolean","MERGE",FACE,{"derivedFrom":[makeQuery(id+"F21.boolean.opBoolean","COPY",FACE,{"derivedFrom":makeQuery(id+"F21.opExtrude","CAP_FACE",FACE,{"disambiguationData":[OSD([sQuery(id+"F6.wireOp",EDGE,"E3.top"),sQuery(id+"F6.wireOp",EDGE,"E3.right"),subQ0])],"isStart":false})}),makeQuery(id+"F23.opExtrude","SWEPT_FACE",FACE,{"disambiguationData":[OSD([subQ3,subQ2,subQ1,subQ0]),TDD([makeQuery(id+"F21.boolean.opBoolean","COPY",EDGE,{"derivedFrom":makeQuery(id+"F21.opExtrude","CAP_EDGE",EDGE,{"disambiguationData":[OSD([subQ3,subQ2,subQ1,subQ0]),TDD([makeQuery(id+"F18.boolean.opBoolean","MERGE",EDGE,{"derivedFrom":[subQ4,makeQuery(id+"F18.opExtrude","SWEPT_EDGE",EDGE,{"disambiguationData":[OSD([subQ3,subQ2,subQ1,subQ0])]})]}),makeQuery(id+"F18.boolean.opBoolean","SPLIT",EDGE,{"derivedFrom":subQ4})])],"isStart":false})})])]})]});}
            extrude(context, id + "F27", {"entities" : qUnion([Q0]), "operationType" : NewBodyOperationType.REMOVE, "oppositeDirection" : true, "depth" : 200 * mm, "offsetDistance" : 25 * mm});
        }
        {
            var Q0;
            {var subQ0=sQuery(id+"F16.wireOp",EDGE,"E5.right");var subQ1=sQuery(id+"F16.wireOp",EDGE,"E5.bottom");var subQ2=sQuery(id+"F4.wireOp",EDGE,"E2.right");var subQ3=sQuery(id+"F4.wireOp",EDGE,"E2.top");var subQ4=makeQuery(id+"F17.boolean.opBoolean","COPY",EDGE,{"derivedFrom":makeQuery(id+"F17.opExtrude","SWEPT_EDGE",EDGE,{"disambiguationData":[OSD([subQ3,subQ2,subQ1,subQ0])]})});Q0=makeQuery(id+"F27.boolean.opBoolean","MERGE",FACE,{"derivedFrom":[makeQuery(id+"F24.opExtrude","CAP_FACE",FACE,{"disambiguationData":[OSD([subQ3,subQ2,subQ1,subQ0])],"isStart":false}),makeQuery(id+"F27.opExtrude","SWEPT_FACE",FACE,{"disambiguationData":[OSD([subQ3,subQ2,subQ1,subQ0]),TDD([makeQuery(id+"F24.opExtrude","CAP_EDGE",EDGE,{"disambiguationData":[OSD([subQ3,subQ2,subQ1,subQ0]),TDD([makeQuery(id+"F23.boolean.opBoolean","COPY",EDGE,{"derivedFrom":makeQuery(id+"F23.opExtrude","CAP_EDGE",EDGE,{"disambiguationData":[OSD([subQ3,subQ2,subQ1,subQ0]),TDD([makeQuery(id+"F21.boolean.opBoolean","COPY",EDGE,{"derivedFrom":makeQuery(id+"F21.opExtrude","CAP_EDGE",EDGE,{"disambiguationData":[OSD([subQ3,subQ2,subQ1,subQ0]),TDD([makeQuery(id+"F18.boolean.opBoolean","MERGE",EDGE,{"derivedFrom":[subQ4,makeQuery(id+"F18.opExtrude","SWEPT_EDGE",EDGE,{"disambiguationData":[OSD([subQ3,subQ2,subQ1,subQ0])]})]}),makeQuery(id+"F18.boolean.opBoolean","SPLIT",EDGE,{"derivedFrom":subQ4})])],"isStart":false})})])],"isStart":false})})])],"isStart":false})])]})]});}
            var Q1;
            Q1=makeQuery(id+"F24.opExtrude","CAP_FACE",FACE,{"disambiguationData":[OSD([sQuery(id+"F16.wireOp",EDGE,"E5.bottom")])],"isStart":false});
            extrude(context, id + "F28", {"entities" : qUnion([Q0, Q1]), "operationType" : NewBodyOperationType.ADD, "depth" : 200 * mm, "offsetDistance" : 25 * mm});
        }
        {
            var Q0;
            {var subQ0=sQuery(id+"F4.wireOp",EDGE,"E2.right");var subQ1=sQuery(id+"F4.wireOp",EDGE,"E2.left");var subQ2=sQuery(id+"F4.wireOp",EDGE,"E2.bottom");var subQ3=sQuery(id+"F4.wireOp",EDGE,"E1.right");var subQ4=sQuery(id+"F4.wireOp",EDGE,"E1.bottom");var subQ5=sQuery(id+"F0.wireOp",EDGE,"E0.left");var subQ6=sQuery(id+"F0.wireOp",EDGE,"E0.bottom");Q0=makeQuery(id+"F26.boolean.opBoolean","MERGE",FACE,{"derivedFrom":[makeQuery(id+"F25.boolean.opBoolean","COPY",FACE,{"derivedFrom":makeQuery(id+"F25.opExtrude","CAP_FACE",FACE,{"disambiguationData":[OSD([subQ6,subQ5,subQ4,subQ3,subQ2,subQ1,subQ0])],"isStart":false})}),makeQuery(id+"F26.opExtrude","SWEPT_FACE",FACE,{"disambiguationData":[OSD([subQ6,subQ5,subQ4,subQ3,subQ2,sQuery(id+"F4.wireOp",EDGE,"E2.top"),subQ1,subQ0,sQuery(id+"F6.wireOp",EDGE,"E3.top"),sQuery(id+"F6.wireOp",EDGE,"E3.left")])]})]});}
            extrude(context, id + "F29", {"entities" : qUnion([Q0]), "operationType" : NewBodyOperationType.REMOVE, "oppositeDirection" : true, "depth" : 200 * mm, "offsetDistance" : 25 * mm});
        }
        {
            var Q0;
            Q0=makeQuery(id+"F29.boolean.opBoolean","COPY",EDGE,{"derivedFrom":makeQuery(id+"F29.opExtrude","CAP_EDGE",EDGE,{"disambiguationData":[OSD([sQuery(id+"F0.wireOp",EDGE,"E0.bottom"),sQuery(id+"F0.wireOp",EDGE,"E0.top"),sQuery(id+"F0.wireOp",EDGE,"E0.left"),sQuery(id+"F0.wireOp",EDGE,"E0.right"),sQuery(id+"F4.wireOp",EDGE,"E1.bottom"),sQuery(id+"F4.wireOp",EDGE,"E1.top"),sQuery(id+"F4.wireOp",EDGE,"E1.left"),sQuery(id+"F4.wireOp",EDGE,"E1.right"),sQuery(id+"F4.wireOp",EDGE,"E2.bottom"),sQuery(id+"F4.wireOp",EDGE,"E2.left"),sQuery(id+"F4.wireOp",EDGE,"E2.right"),sQuery(id+"F6.wireOp",EDGE,"E4.bottom"),sQuery(id+"F6.wireOp",EDGE,"E4.top"),sQuery(id+"F6.wireOp",EDGE,"E4.left"),sQuery(id+"F6.wireOp",EDGE,"E4.right")])],"isStart":false})});
            var Q1;
            {var subQ0=sQuery(id+"F4.wireOp",EDGE,"E1.left");var subQ1=sQuery(id+"F0.wireOp",EDGE,"E0.left");var subQ2=sQuery(id+"F0.wireOp",EDGE,"E0.bottom");Q1=makeQuery(id+"F22.boolean.opBoolean","MERGE",EDGE,{"derivedFrom":[makeQuery(id+"F19.boolean.opBoolean","MERGE",EDGE,{"derivedFrom":[makeQuery(id+"F3.boolean.opBoolean","MERGE",EDGE,{"derivedFrom":[makeQuery(id+"F1.opExtrude","CAP_EDGE",EDGE,{"disambiguationData":[OSD([subQ1])],"isStart":false}),makeQuery(id+"F3.opExtrude","SWEPT_EDGE",EDGE,{"disambiguationData":[OSD([subQ2,subQ1]),TDD([makeQuery(id+"F1.opExtrude","CAP_VERTEX",VERTEX,{"disambiguationData":[OSD([subQ2,subQ1])],"isStart":false})])]})]}),makeQuery(id+"F19.opExtrude","CAP_EDGE",EDGE,{"disambiguationData":[OSD([subQ2,subQ1,sQuery(id+"F6.wireOp",EDGE,"E4.top"),sQuery(id+"F6.wireOp",EDGE,"E4.left")])],"isStart":false}),makeQuery(id+"F19.opExtrude","CAP_EDGE",EDGE,{"disambiguationData":[OSD([subQ2,subQ1,sQuery(id+"F4.wireOp",EDGE,"E1.top"),subQ0])],"isStart":false})]}),makeQuery(id+"F22.opExtrude","SWEPT_EDGE",EDGE,{"disambiguationData":[OSD([sQuery(id+"F4.wireOp",EDGE,"E1.bottom"),subQ0])]})]});}
            var Q2;
            Q2=makeQuery(id+"F19.boolean.opBoolean","COPY",EDGE,{"derivedFrom":makeQuery(id+"F19.opExtrude","CAP_EDGE",EDGE,{"disambiguationData":[OSD([sQuery(id+"F0.wireOp",EDGE,"E0.bottom"),sQuery(id+"F0.wireOp",EDGE,"E0.left"),sQuery(id+"F6.wireOp",EDGE,"E4.bottom"),sQuery(id+"F6.wireOp",EDGE,"E4.right")])],"isStart":false})});
            var Q3;
            {var subQ0=sQuery(id+"F6.wireOp",EDGE,"E3.left");var subQ1=sQuery(id+"F6.wireOp",EDGE,"E3.bottom");Q3=makeQuery(id+"F26.boolean.opBoolean","MERGE",EDGE,{"derivedFrom":[makeQuery(id+"F20.boolean.opBoolean","MERGE",EDGE,{"derivedFrom":[makeQuery(id+"F19.boolean.opBoolean","COPY",EDGE,{"derivedFrom":makeQuery(id+"F19.opExtrude","CAP_EDGE",EDGE,{"disambiguationData":[OSD([sQuery(id+"F0.wireOp",EDGE,"E0.bottom"),sQuery(id+"F0.wireOp",EDGE,"E0.left"),subQ1,sQuery(id+"F6.wireOp",EDGE,"E3.right")])],"isStart":false})}),makeQuery(id+"F20.opExtrude","SWEPT_EDGE",EDGE,{"disambiguationData":[OSD([subQ1,subQ0])]})]}),makeQuery(id+"F26.opExtrude","SWEPT_EDGE",EDGE,{"disambiguationData":[OSD([subQ1,subQ0])]})]});}
            var Q4;
            Q4=makeQuery(id+"F26.opExtrude","CAP_EDGE",EDGE,{"disambiguationData":[OSD([sQuery(id+"F0.wireOp",EDGE,"E0.bottom"),sQuery(id+"F0.wireOp",EDGE,"E0.left"),sQuery(id+"F4.wireOp",EDGE,"E2.bottom"),sQuery(id+"F4.wireOp",EDGE,"E2.top"),sQuery(id+"F4.wireOp",EDGE,"E2.left"),sQuery(id+"F6.wireOp",EDGE,"E3.top"),sQuery(id+"F6.wireOp",EDGE,"E3.left")])],"isStart":false});
            var Q5;
            Q5=makeQuery(id+"F29.boolean.opBoolean","COPY",EDGE,{"derivedFrom":makeQuery(id+"F29.opExtrude","CAP_EDGE",EDGE,{"disambiguationData":[OSD([sQuery(id+"F0.wireOp",EDGE,"E0.bottom"),sQuery(id+"F0.wireOp",EDGE,"E0.top"),sQuery(id+"F0.wireOp",EDGE,"E0.left"),sQuery(id+"F0.wireOp",EDGE,"E0.right"),sQuery(id+"F4.wireOp",EDGE,"E1.bottom"),sQuery(id+"F4.wireOp",EDGE,"E1.right"),sQuery(id+"F4.wireOp",EDGE,"E2.bottom"),sQuery(id+"F4.wireOp",EDGE,"E2.top"),sQuery(id+"F4.wireOp",EDGE,"E2.left"),sQuery(id+"F4.wireOp",EDGE,"E2.right"),sQuery(id+"F6.wireOp",EDGE,"E3.bottom"),sQuery(id+"F6.wireOp",EDGE,"E3.top"),sQuery(id+"F6.wireOp",EDGE,"E3.left"),sQuery(id+"F6.wireOp",EDGE,"E3.right")])],"isStart":false})});
            var Q6;
            {var subQ0=sQuery(id+"F0.wireOp",EDGE,"E0.left");var subQ1=sQuery(id+"F0.wireOp",EDGE,"E0.bottom");Q6=makeQuery(id+"F26.boolean.opBoolean","MERGE",FACE,{"derivedFrom":[makeQuery(id+"F22.boolean.opBoolean","MERGE",FACE,{"derivedFrom":[makeQuery(id+"F20.boolean.opBoolean","MERGE",FACE,{"derivedFrom":[makeQuery(id+"F3.boolean.opBoolean","MERGE",FACE,{"derivedFrom":[makeQuery(id+"F2.boolean.opBoolean","MERGE",FACE,{"derivedFrom":[makeQuery(id+"F1.opExtrude","CAP_FACE",FACE,{"disambiguationData":[OSD([subQ1,sQuery(id+"F0.wireOp",EDGE,"E0.top"),subQ0,sQuery(id+"F0.wireOp",EDGE,"E0.right")])],"isStart":true}),makeQuery(id+"F2.opExtrude","SWEPT_FACE",FACE,{"disambiguationData":[OSD([subQ0]),TDD([makeQuery(id+"F1.opExtrude","CAP_EDGE",EDGE,{"disambiguationData":[OSD([subQ0])],"isStart":true})])]})]}),makeQuery(id+"F3.opExtrude","SWEPT_FACE",FACE,{"disambiguationData":[OSD([subQ1,subQ0]),TDD([makeQuery(id+"F2.boolean.opBoolean","MERGE",EDGE,{"derivedFrom":[makeQuery(id+"F1.opExtrude","CAP_EDGE",EDGE,{"disambiguationData":[OSD([subQ1])],"isStart":true}),makeQuery(id+"F2.opExtrude","SWEPT_EDGE",EDGE,{"disambiguationData":[OSD([subQ1,subQ0]),TDD([makeQuery(id+"F1.opExtrude","CAP_VERTEX",VERTEX,{"disambiguationData":[OSD([subQ1,subQ0])],"isStart":true})])]})]})])]})]}),makeQuery(id+"F20.opExtrude","SWEPT_FACE",FACE,{"disambiguationData":[OSD([subQ1,subQ0])]})]}),makeQuery(id+"F22.opExtrude","SWEPT_FACE",FACE,{"disambiguationData":[OSD([subQ1,subQ0])]})]}),makeQuery(id+"F26.opExtrude","SWEPT_FACE",FACE,{"disambiguationData":[OSD([subQ1,subQ0])]})]});}
            chamfer(context, id + "F30", {"entities" : qUnion([Q0, Q1, Q2, Q3, Q4, Q5, Q6]), "width" : 1 * mm, "tangentPropagation" : true});
        }
    });
